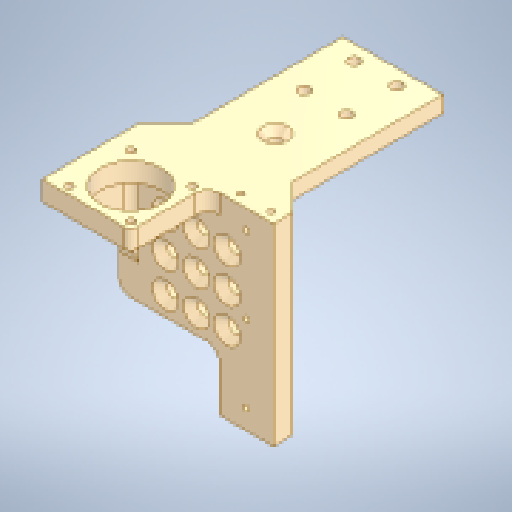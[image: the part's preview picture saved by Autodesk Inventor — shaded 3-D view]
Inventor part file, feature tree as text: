
AUTODESK INVENTOR PART (.ipt)
format: ipt  version: 2024.1 (Build 281209000, 209)  size: 382,464 bytes
history: native  units: in
note: dims shown in document units (in); Inventor stores cm internally (conversion verified against a paired STEP export)
features: extrude x12, sketch x12, fillet x6, chamfer x4, mirror x1
ambient origin geometry x8: Origin, YZ Plane, XZ Plane, XY Plane, X Axis, Y Axis, Z Axis, Center Point
bodies: Solid1 (feature_tree)
feature tree (35):
  extrude  "Extrusion1"  Depth=1.378in
  extrude  "Extrusion2"  Depth=0.1969in
  extrude  "Extrusion3"  Depth=0.1969in TaperAngle=0.0deg
  extrude  "Extrusion4"  Depth=0.1181in
  fillet  "Fillet1"  Radius=0.7874in
  extrude  "Extrusion5"  Depth=0.3937in
  fillet  "Fillet2"  Radius=0.3937in
  fillet  "Fillet4"  Radius=0.0787in
  extrude  "Extrusion6"  Depth=0.0787in
  chamfer  "Chamfer2"  Distance=0.315in
  extrude  "Extrusion7"  Depth=0.315in
  chamfer  "Chamfer3"  Distance=0.315in
  extrude  "Extrusion8"  TaperAngle=0.0deg  [1 undecoded]
  chamfer  "Chamfer4"  Distance=0.0591in
  fillet  "Fillet5"  [1 undecoded]
  extrude  "Extrusion9"  Depth=0.1969in
  extrude  "Extrusion10"  Depth=0.0787in
  fillet  "Fillet6"  Radius=0.1969in
  extrude  "Extrusion11"  Depth=0.1181in
  chamfer  "Chamfer7"  Distance=0.2756in
  extrude  "Extrusion12"  Depth=0.1181in TaperAngle=0.0deg
  fillet  "Fillet7"  Radius=0.0787in
  mirror  "Mirror1"
  sketch  "Sketch1"  dims[d0=1.5748in d1=1.378in]
  sketch  "Sketch2"  dims[d2=0.1969in d3=0.0in d4=0.9055in]
  sketch  "Sketch3"  dims[d5=0.1969in d6=0.7874in d7=0.0in]
  sketch  "Sketch4"  dims[d8=0.7874in d9=0.1181in d10=0.7874in d11=0.0in]
  sketch  "Sketch5"  dims[d12=0.6299in d13=0.3937in d14=0.3937in d15=0.0787in]
  sketch  "Sketch6"  dims[d16=0.0787in d17=0.0787in]
  sketch  "Sketch7"  dims[d18=0.0787in]
  sketch  "Sketch8"  dims[d19=0.315in]
  sketch  "Sketch9"  dims[d20=0.315in]
  sketch  "Sketch10"  dims[d21=0.315in]
  sketch  "Sketch11"  dims[d22=0.315in]
  sketch  "Sketch12"  dims[d23=0.315in d24=0.315in d25=0.315in d26=0.315in d27=0.0in d28=0.0in d29=0.0591in d30=0.0in d31=0.0in d32=0.1969in d34=0.0787in d39=0.1969in d40=0.2756in d41=0.2756in d42=1.811in d43=0.0in d44=0.2756in d45=0.0787in d46=45.0deg d47=0.1181in d48=0.6102in d49=0.5118in d50=0.0in d51=0.0in d52=0.0709in d53=0.0787in d54=45.0deg d55=0.063in d56=0.063in d57=0.0984in d58=0.0984in d59=0.1181in d60=0.315in d61=0.3937in d62=0.0in d63=0.0315in d64=0.0787in d65=45.0deg d66=0.0394in d67=0.5512in d68=0.5906in d69=0.0in d70=0.063in d71=0.2756in d72=0.1969in d73=1.1811in d75=0.7874in d76=0.3937in d78=0.3937in d80=0.0in d81=0.0in d88=0.1181in d89=0.1181in d90=0.1181in d91=0.1181in d92=0.1181in d93=0.1181in d94=0.1181in d95=0.1969in d96=0.1969in d97=0.315in d98=0.4724in d99=0.4724in d100=0.4724in d101=0.3543in d102=0.3543in d103=0.3543in d104=0.315in d105=0.3543in d106=0.315in d107=0.0in d108=0.0in d109=0.315in d110=0.1181in d111=0.1969in d112=0.3543in d113=0.3543in d114=0.1181in d115=0.1181in d116=0.315in d117=0.315in d118=0.0748in d119=0.0787in d120=45.0deg d121=0.1181in d122=0.1181in d123=0.1181in d124=0.1181in d125=0.6693in d126=0.6693in d127=0.315in d128=0.315in d129=0.2756in d130=0.2756in d131=0.1575in d132=0.1575in d133=0.0in d134=0.0in d138=0.1181in]
note: 2 required parameter values undecoded (feature->parameter linkage not recoverable at this tier; creation-order binding heuristic only, values carry confidence <= 0.55)
